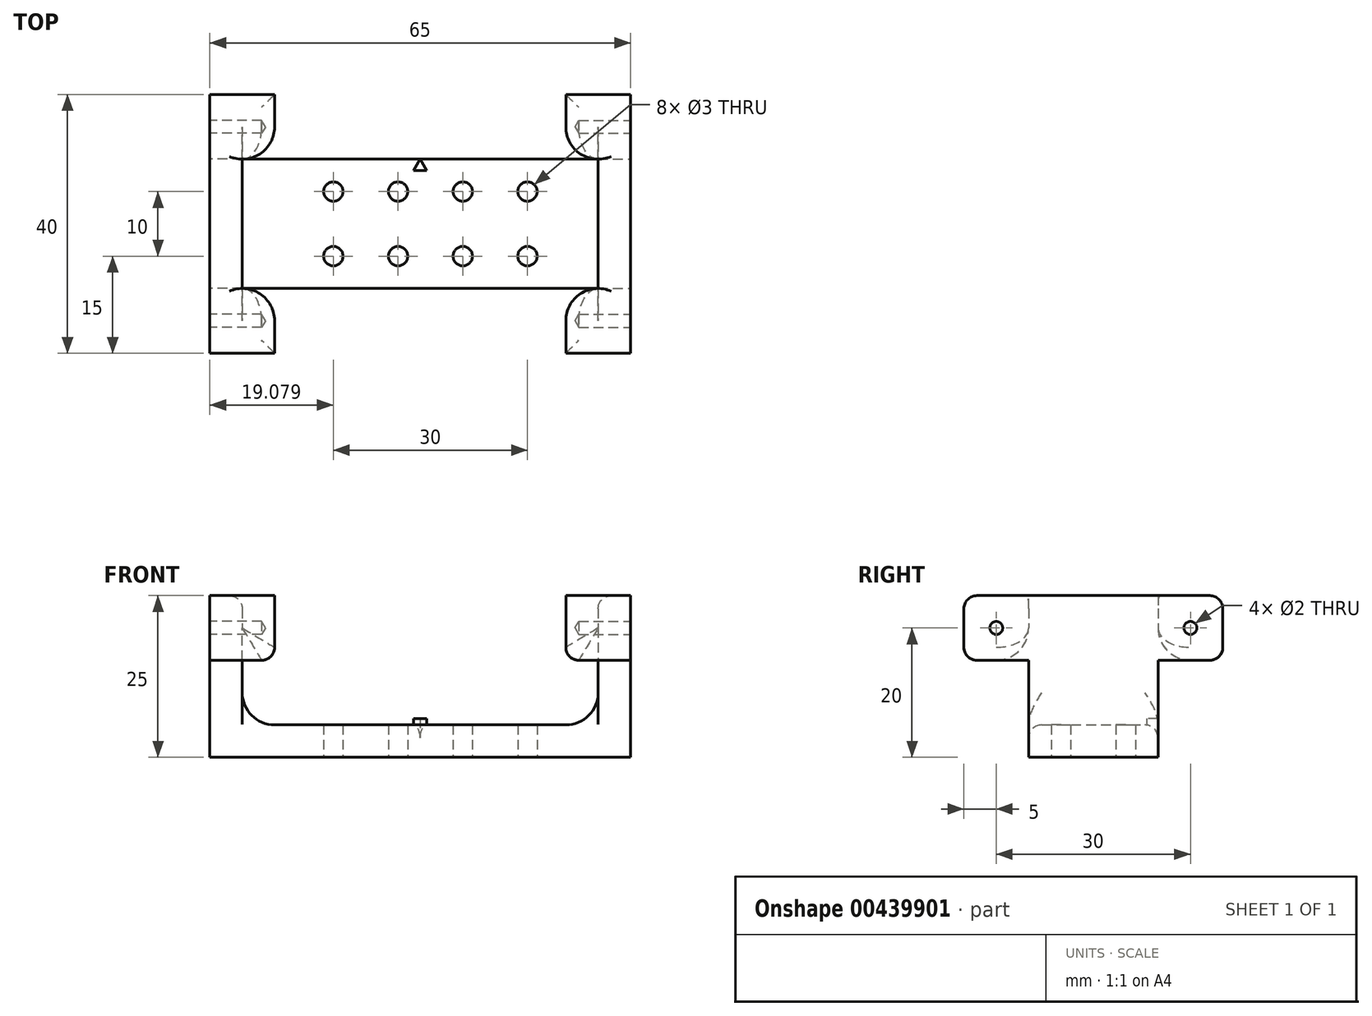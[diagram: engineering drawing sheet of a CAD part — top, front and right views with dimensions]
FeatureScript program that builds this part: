
annotation { "Feature Type Name" : "Feature", "Feature Type Description" : "" }
export const myFeature = defineFeature(function(context is Context, id is Id, definition is map)
    precondition{}
    {
        {
            var Q0;
            Q0=qCreatedBy(makeId("Front.planeOp"),FACE);
            var sketch = newSketch(context, id + "F0", { "sketchPlane" : qUnion([Q0])});
            skLineSegment(sketch, "E0.bottom", {"start": v(-32.5, 25) * mm, "end": v(-27.5, 25) * mm});
            skLineSegment(sketch, "E0.top", {"start": v(-27.5, 5) * mm, "end": v(27.5, 5) * mm});
            skLineSegment(sketch, "E0.left", {"start": v(-27.5, 25) * mm, "end": v(-27.5, 5) * mm});
            skLineSegment(sketch, "E0.right", {"start": v(27.5, 25) * mm, "end": v(27.5, 5) * mm});
            skLineSegment(sketch, "E1", {"start": v(-32.5, 25) * mm, "end": v(-32.5, 0) * mm});
            skLineSegment(sketch, "E2", {"start": v(32.5, 25) * mm, "end": v(32.5, 0) * mm});
            skLineSegment(sketch, "E3.trimOffspring", {"start": v(27.5, 25) * mm, "end": v(32.5, 25) * mm});
            skLineSegment(sketch, "E4", {"start": v(-32.5, 0) * mm, "end": v(32.5, 0) * mm});
            skSolve(sketch);
        }
        {
            var Q0;
            Q0=qSketchRegion(id+"F0",true);
            extrude(context, id + "F1", {"entities" : qUnion([Q0]), "endBound" : BoundingType.SYMMETRIC, "depth" : 20 * mm, "offsetDistance" : 25 * mm});
        }
        {
            var Q0;
            Q0=makeQuery(id+"F1.opExtrude","SWEPT_FACE",FACE,{"disambiguationData":[OSD([sQuery(id+"F0.wireOp",EDGE,"E4")])]});
            var sketch = newSketch(context, id + "F2", { "sketchPlane" : qUnion([Q0])});
            skCircle(sketch, "E5", {"center": v(-13.42, 5) * mm, "radius": 1.24 * mm});
            skCircle(sketch, "E6.0.1.0", {"center": v(-13.42, -5) * mm, "radius": 1.24 * mm});
            skCircle(sketch, "E6.1.0.0", {"center": v(-3.42, 5) * mm, "radius": 1.24 * mm});
            skCircle(sketch, "E6.1.1.0", {"center": v(-3.42, -5) * mm, "radius": 1.24 * mm});
            skCircle(sketch, "E6.2.0.0", {"center": v(6.58, 5) * mm, "radius": 1.24 * mm});
            skCircle(sketch, "E6.2.1.0", {"center": v(6.58, -5) * mm, "radius": 1.24 * mm});
            skCircle(sketch, "E6.3.0.0", {"center": v(16.58, 5) * mm, "radius": 1.24 * mm});
            skCircle(sketch, "E6.3.1.0", {"center": v(16.58, -5) * mm, "radius": 1.24 * mm});
            skLineSegment(sketch, "E7", {"start": v(-32.5, 0) * mm, "end": v(32.5, 0) * mm, "construction": true});
            skLineSegment(sketch, "E8", {"start": v(-13.42, 5) * mm, "end": v(-32.5, 0) * mm, "construction": true});
            skLineSegment(sketch, "E9", {"start": v(-13.42, -5) * mm, "end": v(-32.5, 0) * mm, "construction": true});
            skLineSegment(sketch, "E10", {"start": v(16.58, 5) * mm, "end": v(32.5, 0) * mm, "construction": true});
            skLineSegment(sketch, "E11", {"start": v(32.5, 0) * mm, "end": v(16.58, -5) * mm, "construction": true});
            skSolve(sketch);
        }
        {
            var Q0;
            Q0=makeQuery(id+"F1.opExtrude","SWEPT_FACE",FACE,{"disambiguationData":[OSD([sQuery(id+"F0.wireOp",EDGE,"E0.top")])]});
            var sketch = newSketch(context, id + "F3", { "sketchPlane" : qUnion([Q0])});
            skLineSegment(sketch, "E12", {"start": v(0, 0) * mm, "end": v(0, 14.1) * mm, "construction": true});
            skLineSegment(sketch, "E13", {"start": v(0, 10) * mm, "end": v(-1, 8.27) * mm});
            skLineSegment(sketch, "E14", {"start": v(-1, 8.27) * mm, "end": v(1, 8.27) * mm});
            skLineSegment(sketch, "E15", {"start": v(0, 10) * mm, "end": v(1, 8.27) * mm});
            skSolve(sketch);
        }
        {
            var Q0;
            Q0 = qSketchRegion(id + "F3", true);
            extrude(context, id + "F4", {"entities" : qUnion([Q0]), "operationType" : NewBodyOperationType.ADD, "depth" : 1 * mm, "offsetDistance" : 25 * mm});
        }
        {
            var Q0;
            Q0=makeQuery(id+"F1.opExtrude","SWEPT_FACE",FACE,{"disambiguationData":[OSD([sQuery(id+"F0.wireOp",EDGE,"E1")])]});
            var sketch = newSketch(context, id + "F5", { "sketchPlane" : qUnion([Q0])});
            skLineSegment(sketch, "E16", {"start": v(-20, 25) * mm, "end": v(20, 25) * mm});
            skLineSegment(sketch, "E17.0", {"start": v(-20, 15) * mm, "end": v(20, 15) * mm});
            skLineSegment(sketch, "E18", {"start": v(-20, 25) * mm, "end": v(-20, 15) * mm});
            skLineSegment(sketch, "E19", {"start": v(20, 25) * mm, "end": v(20, 15) * mm});
            skLineSegment(sketch, "E20", {"start": v(-20, 20) * mm, "end": v(20, 20) * mm, "construction": true});
            skLineSegment(sketch, "E21.0", {"start": v(-15, 25) * mm, "end": v(-15, 15) * mm, "construction": true});
            skLineSegment(sketch, "E22.MirrorCS", {"start": v(15, 25) * mm, "end": v(15, 15) * mm, "construction": true});
            skPoint(sketch, "E23", {"position": v(-15, 20) * mm});
            skPoint(sketch, "E24", {"position": v(15, 20) * mm});
            skSolve(sketch);
        }
        {
            var Q0;
            {var subQ3=sQuery(id+"F5.wireOp",EDGE,"E18");Q0=makeQuery(id+"F5.imprint","IMPRINT",FACE,{"disambiguationData":[TD([[makeQuery(id+"F5.imprint","IMPRINT",EDGE,{"derivedFrom":subQ3}),1.0]])]});}
            var Q1;
            {var subQ3=sQuery(id+"F5.wireOp",EDGE,"E19");Q1=makeQuery(id+"F5.imprint","IMPRINT",FACE,{"disambiguationData":[TD([[makeQuery(id+"F5.imprint","IMPRINT",EDGE,{"derivedFrom":subQ3}),-1.0]])]});}
            var Q2;
            Q2=sQuery(id+"F5.wireOp",EDGE,"E16");
            var Q3;
            Q3=sQuery(id+"F5.wireOp",EDGE,"E18");
            var Q4;
            Q4=sQuery(id+"F5.wireOp",EDGE,"E17.0");
            var Q5;
            Q5=sQuery(id+"F5.wireOp",EDGE,"E19");
            extrude(context, id + "F6", {"entities" : qUnion([Q0, Q1]), "operationType" : NewBodyOperationType.ADD, "surfaceEntities" : qUnion([Q2, Q3, Q4, Q5]), "oppositeDirection" : true, "depth" : 10 * mm, "offsetDistance" : 25 * mm});
        }
        {
            var Q0;
            Q0=sQuery(id+"F5.wireOp",VERTEX,"E23");
            var Q1;
            Q1=sQuery(id+"F5.wireOp",VERTEX,"E24");
            var Q2;
            Q2=makeQuery(id+"F1.opExtrude","SWEPT_BODY",BODY,{"disambiguationData":[OSD([sQuery(id+"F0.wireOp",EDGE,"E0.bottom"),sQuery(id+"F0.wireOp",EDGE,"E0.top"),sQuery(id+"F0.wireOp",EDGE,"E0.left"),sQuery(id+"F0.wireOp",EDGE,"E0.right"),sQuery(id+"F0.wireOp",EDGE,"E1"),sQuery(id+"F0.wireOp",EDGE,"E2"),sQuery(id+"F0.wireOp",EDGE,"E3.trimOffspring"),sQuery(id+"F0.wireOp",EDGE,"E4")])]});
            hole(context, id + "F7", {"style" : HoleStyle.SIMPLE, "endStyle" : HoleEndStyle.BLIND, "holeDiameter" : 2 * mm, "majorDiameter" : 5 * mm, "holeDepth" : 8 * mm, "isTappedThrough" : true, "tappedDepth" : 12 * mm, "tapClearance" : 3, "startFromSketch" : true, "locations" : qUnion([Q0, Q1]), "scope" : qUnion([Q2])});
        }
        {
            var Q0;
            Q0=makeQuery(id+"F6.opExtrude","SWEPT_EDGE",EDGE,{"disambiguationData":[OSD([sQuery(id+"F5.wireOp",EDGE,"E16"),sQuery(id+"F5.wireOp",EDGE,"E19")])]});
            var Q1;
            Q1=makeQuery(id+"F6.opExtrude","SWEPT_EDGE",EDGE,{"disambiguationData":[OSD([sQuery(id+"F5.wireOp",EDGE,"E16"),sQuery(id+"F5.wireOp",EDGE,"E18")])]});
            var Q2;
            Q2=makeQuery(id+"F6.opExtrude","SWEPT_EDGE",EDGE,{"disambiguationData":[OSD([sQuery(id+"F5.wireOp",EDGE,"E17.0"),sQuery(id+"F5.wireOp",EDGE,"E18")])]});
            var Q3;
            {var subQ0=sQuery(id+"F5.wireOp",EDGE,"E17.0");Q3=makeQuery(id+"F6.opExtrude","CAP_EDGE",EDGE,{"disambiguationData":[OSD([subQ0]),TDD([makeQuery(id+"F5.imprint","IMPRINT",EDGE,{"disambiguationData":[TD([[makeQuery(id+"F5.imprint","INTERSECT",VERTEX,{"derivedFrom":[subQ0,sQuery(id+"F5.wireOp",EDGE,"E18")]}),-1.0]])],"derivedFrom":subQ0})])],"isStart":false});}
            var Q4;
            {var subQ0=sQuery(id+"F5.wireOp",EDGE,"E17.0");Q4=makeQuery(id+"F6.opExtrude","CAP_EDGE",EDGE,{"disambiguationData":[OSD([subQ0]),TDD([makeQuery(id+"F5.imprint","IMPRINT",EDGE,{"disambiguationData":[TD([[makeQuery(id+"F5.imprint","INTERSECT",VERTEX,{"derivedFrom":[subQ0,sQuery(id+"F5.wireOp",EDGE,"E19")]}),1.0]])],"derivedFrom":subQ0})])],"isStart":false});}
            var Q5;
            Q5=makeQuery(id+"F6.opExtrude","SWEPT_EDGE",EDGE,{"disambiguationData":[OSD([sQuery(id+"F5.wireOp",EDGE,"E17.0"),sQuery(id+"F5.wireOp",EDGE,"E19")])]});
            fillet(context, id + "F8", {"entities" : qUnion([Q0, Q1, Q2, Q3, Q4, Q5]), "radius" : 2 * mm, "tangentPropagation" : true, "allowEdgeOverflow" : false});
        }
        {
            var Q0;
            {var subQ0=sQuery(id+"F0.wireOp",EDGE,"E1");var subQ1=sQuery(id+"F5.wireOp",EDGE,"E17.0");var subQ2=makeQuery(id+"F5.imprint","INTERSECT",VERTEX,{"derivedFrom":[makeQuery(id+"F1.opExtrude","CAP_EDGE",EDGE,{"disambiguationData":[OSD([subQ0])],"isStart":false}),subQ1]});Q0=makeQuery(id+"F6.boolean.opBoolean","SPLIT",EDGE,{"disambiguationData":[topologyDisambiguationEdgeConnected([makeQuery(id+"F1.opExtrude","CAP_FACE",FACE,{"disambiguationData":[OSD([sQuery(id+"F0.wireOp",EDGE,"E0.bottom"),sQuery(id+"F0.wireOp",EDGE,"E0.top"),sQuery(id+"F0.wireOp",EDGE,"E0.left"),sQuery(id+"F0.wireOp",EDGE,"E0.right"),subQ0,sQuery(id+"F0.wireOp",EDGE,"E2"),sQuery(id+"F0.wireOp",EDGE,"E3.trimOffspring"),sQuery(id+"F0.wireOp",EDGE,"E4")])],"isStart":false})])],"derivedFrom":makeQuery(id+"F6.opExtrude","SWEPT_EDGE",EDGE,{"disambiguationData":[OSD([subQ0,subQ1]),TDD([subQ2])]})});}
            var Q1;
            {var subQ0=sQuery(id+"F0.wireOp",EDGE,"E1");var subQ1=sQuery(id+"F5.wireOp",EDGE,"E17.0");var subQ2=makeQuery(id+"F5.imprint","INTERSECT",VERTEX,{"derivedFrom":[makeQuery(id+"F1.opExtrude","CAP_EDGE",EDGE,{"disambiguationData":[OSD([subQ0])],"isStart":true}),subQ1]});Q1=makeQuery(id+"F6.boolean.opBoolean","SPLIT",EDGE,{"disambiguationData":[topologyDisambiguationEdgeConnected([makeQuery(id+"F1.opExtrude","CAP_FACE",FACE,{"disambiguationData":[OSD([sQuery(id+"F0.wireOp",EDGE,"E0.bottom"),sQuery(id+"F0.wireOp",EDGE,"E0.top"),sQuery(id+"F0.wireOp",EDGE,"E0.left"),sQuery(id+"F0.wireOp",EDGE,"E0.right"),subQ0,sQuery(id+"F0.wireOp",EDGE,"E2"),sQuery(id+"F0.wireOp",EDGE,"E3.trimOffspring"),sQuery(id+"F0.wireOp",EDGE,"E4")])],"isStart":true})])],"derivedFrom":makeQuery(id+"F6.opExtrude","SWEPT_EDGE",EDGE,{"disambiguationData":[OSD([subQ0,subQ1]),TDD([subQ2])]})});}
            var Q2;
            Q2=makeQuery(id+"F1.opExtrude","SWEPT_EDGE",EDGE,{"disambiguationData":[OSD([sQuery(id+"F0.wireOp",EDGE,"E0.top"),sQuery(id+"F0.wireOp",EDGE,"E0.left")])]});
            fillet(context, id + "F9", {"entities" : qUnion([Q0, Q1, Q2]), "radius" : 5 * mm, "tangentPropagation" : true, "allowEdgeOverflow" : false});
        }
        {
            var Q0;
            {var subQ0=sQuery(id+"F0.wireOp",EDGE,"E0.left");var subQ1=sQuery(id+"F0.wireOp",EDGE,"E1");var subQ2=makeQuery(id+"F1.opExtrude","CAP_EDGE",EDGE,{"disambiguationData":[OSD([subQ1])],"isStart":true});Q0=makeQuery(id+"F6.boolean.opBoolean","SPLIT",EDGE,{"disambiguationData":[topologyDisambiguationEdgeConnected([makeQuery(id+"F6.opExtrude","SWEPT_FACE",FACE,{"disambiguationData":[OSD([subQ1]),TDD([makeQuery(id+"F5.imprint","IMPRINT",EDGE,{"disambiguationData":[TD([[makeQuery(id+"F5.imprint","INTERSECT",VERTEX,{"derivedFrom":[subQ2,sQuery(id+"F5.wireOp",EDGE,"E16")]}),-1.0]])],"derivedFrom":subQ2})])]})])],"derivedFrom":makeQuery(id+"F1.opExtrude","CAP_EDGE",EDGE,{"disambiguationData":[OSD([subQ0])],"isStart":true})});}
            var Q1;
            {var subQ0=sQuery(id+"F0.wireOp",EDGE,"E0.left");var subQ1=sQuery(id+"F0.wireOp",EDGE,"E1");var subQ2=makeQuery(id+"F1.opExtrude","CAP_EDGE",EDGE,{"disambiguationData":[OSD([subQ1])],"isStart":false});Q1=makeQuery(id+"F6.boolean.opBoolean","SPLIT",EDGE,{"disambiguationData":[topologyDisambiguationEdgeConnected([makeQuery(id+"F6.opExtrude","SWEPT_FACE",FACE,{"disambiguationData":[OSD([subQ1]),TDD([makeQuery(id+"F5.imprint","IMPRINT",EDGE,{"disambiguationData":[TD([[makeQuery(id+"F5.imprint","INTERSECT",VERTEX,{"derivedFrom":[subQ2,sQuery(id+"F5.wireOp",EDGE,"E16")]}),-1.0]])],"derivedFrom":subQ2})])]})])],"derivedFrom":makeQuery(id+"F1.opExtrude","CAP_EDGE",EDGE,{"disambiguationData":[OSD([subQ0])],"isStart":false})});}
            fillet(context, id + "F10", {"entities" : qUnion([Q0, Q1]), "radius" : 2 * mm, "tangentPropagation" : true, "allowEdgeOverflow" : false});
        }
        {
            var Q0;
            Q0=makeQuery(id+"F1.opExtrude","SWEPT_BODY",BODY,{"disambiguationData":[OSD([sQuery(id+"F0.wireOp",EDGE,"E0.bottom"),sQuery(id+"F0.wireOp",EDGE,"E0.top"),sQuery(id+"F0.wireOp",EDGE,"E0.left"),sQuery(id+"F0.wireOp",EDGE,"E0.right"),sQuery(id+"F0.wireOp",EDGE,"E1"),sQuery(id+"F0.wireOp",EDGE,"E2"),sQuery(id+"F0.wireOp",EDGE,"E3.trimOffspring"),sQuery(id+"F0.wireOp",EDGE,"E4")])]});
            var Q1;
            Q1=qCreatedBy(makeId("Right.planeOp"),FACE);
            mirror(context, id + "F11", {"operationType" : NewBodyOperationType.ADD, "entities" : qUnion([Q0]), "mirrorPlane" : qUnion([Q1])});
        }
        {
            var Q0;
            Q0=sQuery(id+"F2.wireOp",VERTEX,"E5.center");
            var Q1;
            Q1=sQuery(id+"F2.wireOp",VERTEX,"E6.1.0.0.center");
            var Q2;
            Q2=sQuery(id+"F2.wireOp",VERTEX,"E6.2.0.0.center");
            var Q3;
            Q3=sQuery(id+"F2.wireOp",VERTEX,"E6.3.0.0.center");
            var Q4;
            Q4=sQuery(id+"F2.wireOp",VERTEX,"E6.0.1.0.center");
            var Q5;
            Q5=sQuery(id+"F2.wireOp",VERTEX,"E6.1.1.0.center");
            var Q6;
            Q6=sQuery(id+"F2.wireOp",VERTEX,"E6.2.1.0.center");
            var Q7;
            Q7=sQuery(id+"F2.wireOp",VERTEX,"E6.3.1.0.center");
            var Q8;
            Q8=makeQuery(id+"F1.opExtrude","SWEPT_BODY",BODY,{"disambiguationData":[OSD([sQuery(id+"F0.wireOp",EDGE,"E0.bottom"),sQuery(id+"F0.wireOp",EDGE,"E0.top"),sQuery(id+"F0.wireOp",EDGE,"E0.left"),sQuery(id+"F0.wireOp",EDGE,"E0.right"),sQuery(id+"F0.wireOp",EDGE,"E1"),sQuery(id+"F0.wireOp",EDGE,"E2"),sQuery(id+"F0.wireOp",EDGE,"E3.trimOffspring"),sQuery(id+"F0.wireOp",EDGE,"E4")])]});
            hole(context, id + "F12", {"style" : HoleStyle.SIMPLE, "endStyle" : HoleEndStyle.THROUGH, "holeDiameter" : 3 * mm, "isTappedThrough" : true, "tappedDepth" : 12 * mm, "tapClearance" : 3, "startFromSketch" : true, "locations" : qUnion([Q0, Q1, Q2, Q3, Q4, Q5, Q6, Q7]), "scope" : qUnion([Q8]), "majorDiameter" : 5 * mm});
        }
        {
            var Q0;
            Q0=makeQuery(id+"F1.opExtrude","SWEPT_EDGE",EDGE,{"disambiguationData":[OSD([sQuery(id+"F0.wireOp",EDGE,"E0.bottom"),sQuery(id+"F0.wireOp",EDGE,"E0.left")])]});
            var Q1;
            Q1=makeQuery(id+"F1.opExtrude","SWEPT_EDGE",EDGE,{"disambiguationData":[OSD([sQuery(id+"F0.wireOp",EDGE,"E0.right"),sQuery(id+"F0.wireOp",EDGE,"E3.trimOffspring")])]});
            fillet(context, id + "F13", {"entities" : qUnion([Q0, Q1]), "radius" : 2 * mm, "tangentPropagation" : true, "allowEdgeOverflow" : false});
        }
    });
